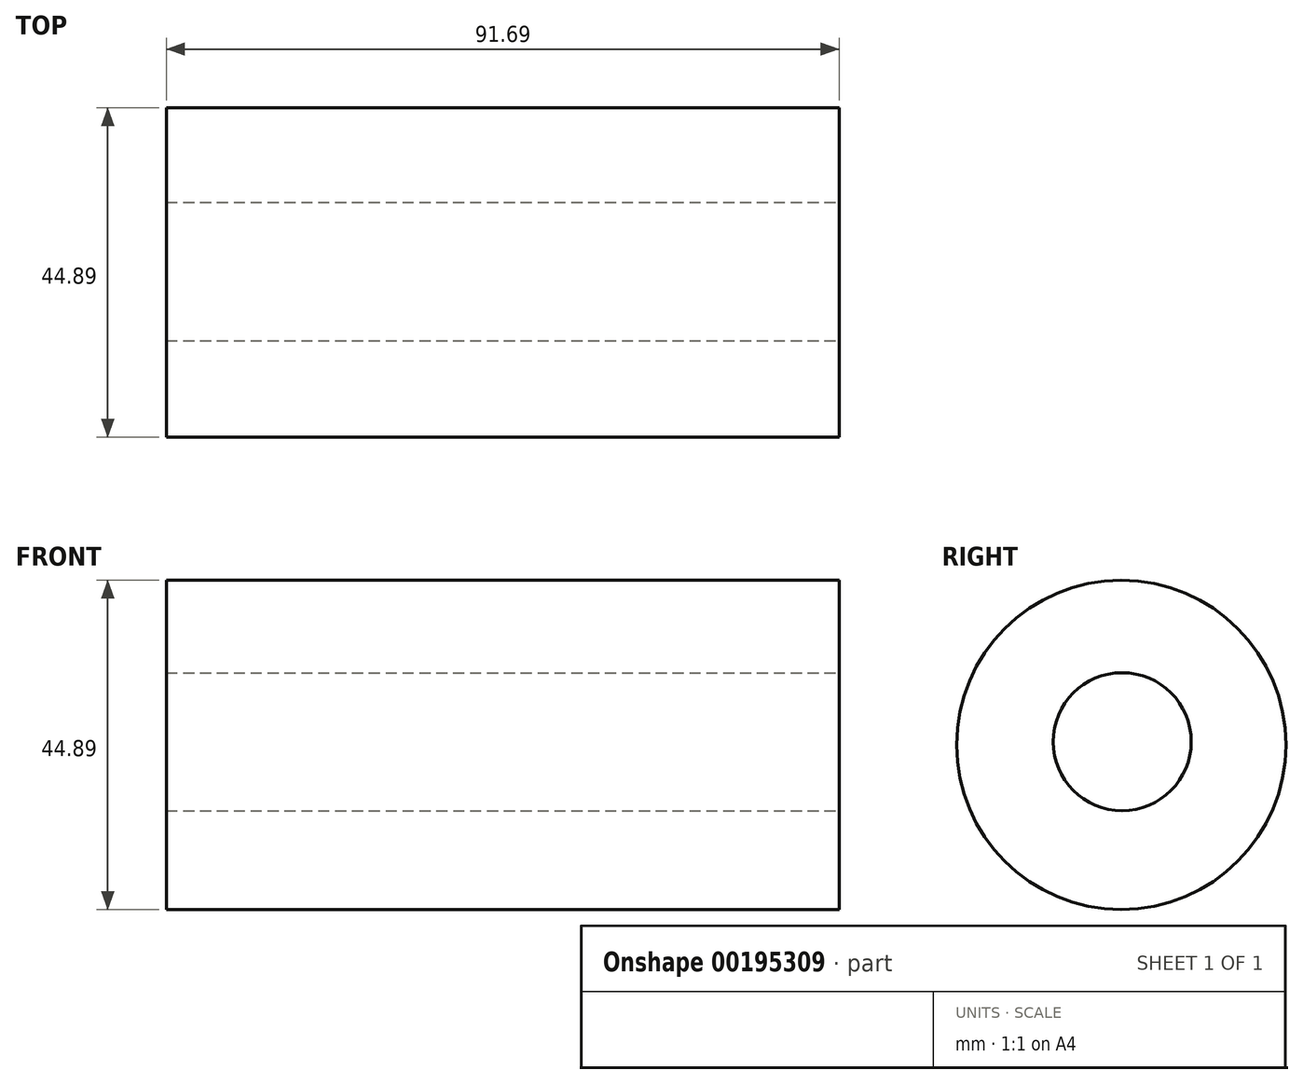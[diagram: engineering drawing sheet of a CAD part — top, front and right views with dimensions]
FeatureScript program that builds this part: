
annotation { "Feature Type Name" : "Feature", "Feature Type Description" : "" }
export const myFeature = defineFeature(function(context is Context, id is Id, definition is map)
    precondition{}
    {
        {
            var Q0;
            Q0=qCreatedBy(makeId("Right.planeOp"),FACE);
            var sketch = newSketch(context, id + "F0", { "sketchPlane" : qUnion([Q0])});
            skCircle(sketch, "E0", {"center": v(-27.57, 36.44) * mm, "radius": 22.44 * mm});
            skSolve(sketch);
        }
        {
            var Q0;
            Q0=makeQuery(id+"F0.imprint","IMPRINT",FACE,{"disambiguationData":[TD([[makeQuery(id+"F0.imprint","IMPRINT",EDGE,{"derivedFrom":sQuery(id+"F0.wireOp",EDGE,"E0")}),1.0]])]});
            var sketch = newSketch(context, id + "F1", { "sketchPlane" : qUnion([Q0])});
            skCircle(sketch, "E1", {"center": v(-27.45, 36.87) * mm, "radius": 9.4 * mm});
            skSolve(sketch);
        }
        {
            var Q0;
            Q0 = qSketchRegion(id + "F1", true);
            var Q1;
            Q1=makeQuery(id+"F0.imprint","IMPRINT",FACE,{"disambiguationData":[TD([[makeQuery(id+"F0.imprint","IMPRINT",EDGE,{"derivedFrom":sQuery(id+"F0.wireOp",EDGE,"E0")}),1.0]])]});
            extrude(context, id + "F2", {"entities" : qUnion([Q0, Q1]), "oppositeDirection" : true, "depth" : 91.7 * mm});
        }
    });
